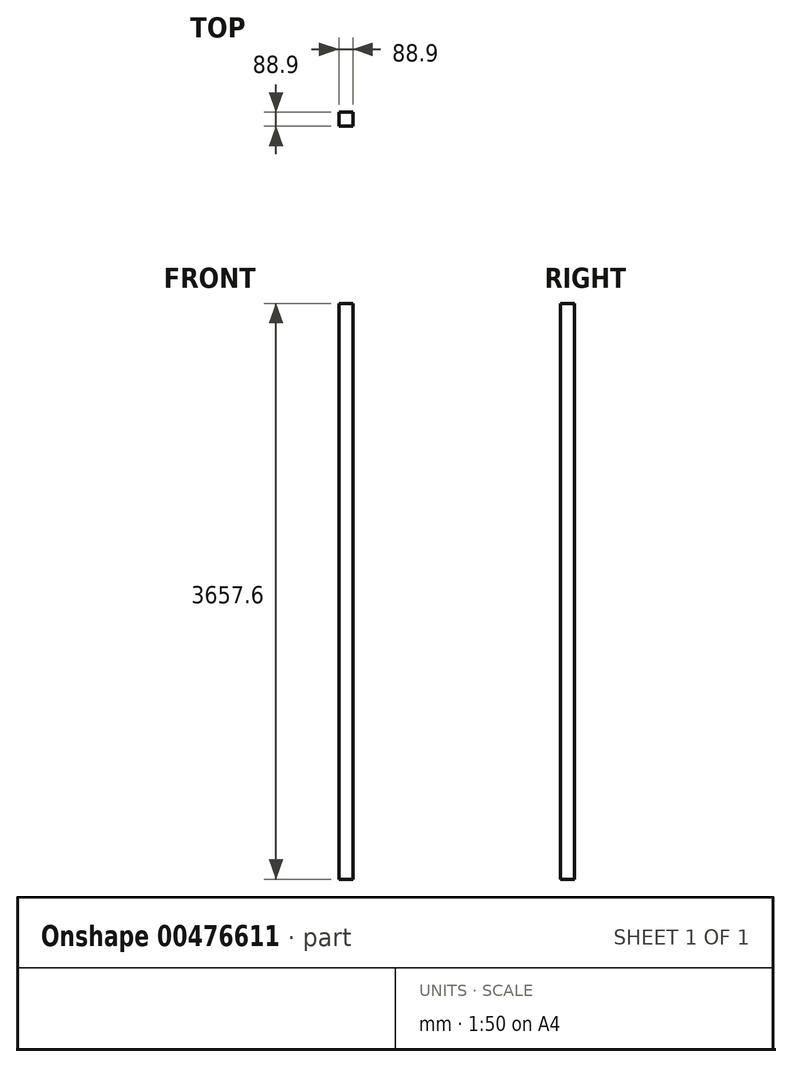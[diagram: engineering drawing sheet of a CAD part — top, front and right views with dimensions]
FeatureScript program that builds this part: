
annotation { "Feature Type Name" : "Feature", "Feature Type Description" : "" }
export const myFeature = defineFeature(function(context is Context, id is Id, definition is map)
    precondition{}
    {
        {
            var Q0;
            Q0=qCreatedBy(makeId("Top.planeOp"),FACE);
            var sketch = newSketch(context, id + "F0", { "sketchPlane" : qUnion([Q0])});
            skLineSegment(sketch, "E0.bottom", {"start": v(-97.98, 0.6) * mm, "end": v(-9.08, 0.6) * mm});
            skLineSegment(sketch, "E0.top", {"start": v(-97.98, -88.3) * mm, "end": v(-9.08, -88.3) * mm});
            skLineSegment(sketch, "E0.left", {"start": v(-97.98, 0.6) * mm, "end": v(-97.98, -88.3) * mm});
            skLineSegment(sketch, "E0.right", {"start": v(-9.08, 0.6) * mm, "end": v(-9.08, -88.3) * mm});
            skSolve(sketch);
        }
        {
            var Q0;
            Q0=makeQuery(id+"F0.imprint","IMPRINT",FACE,{"disambiguationData":[TD([[makeQuery(id+"F0.imprint","IMPRINT",EDGE,{"derivedFrom":sQuery(id+"F0.wireOp",EDGE,"E0.bottom")}),-1.0]])]});
            var Q1;
            Q1=sQuery(id+"F0.wireOp",EDGE,"E0.left");
            var Q2;
            Q2=sQuery(id+"F0.wireOp",EDGE,"E0.top");
            var Q3;
            Q3=sQuery(id+"F0.wireOp",EDGE,"E0.right");
            var Q4;
            Q4=sQuery(id+"F0.wireOp",EDGE,"E0.bottom");
            extrude(context, id + "F1", {"entities" : qUnion([Q0]), "surfaceEntities" : qUnion([Q1, Q2, Q3, Q4]), "depth" : 3657.6 * mm});
        }
    });
